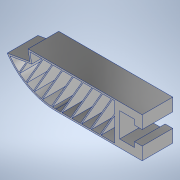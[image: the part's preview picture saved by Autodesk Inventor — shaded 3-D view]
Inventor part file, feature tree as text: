
AUTODESK INVENTOR PART (.ipt)
format: ipt  version: 2022 (Build 260153000, 153)  size: 298,496 bytes
history: native  units: mm
features: extrude x5, sketch x3, fillet x1, shell x1, projected_geometry x1
ambient origin geometry x8: Origin, YZ Plane, XZ Plane, XY Plane, X Axis, Y Axis, Z Axis, Center Point
bodies: Body1 (feature_tree)
feature tree (11):
  extrude  "Extrusion2"  Depth=5.8mm
  extrude  "Extrusion5"  Depth=12.0mm TaperAngle=0.0deg
  fillet  "Fillet2"  Radius=45.0mm
  shell  "Shell1"  Thickness=15.6mm
  extrude  "Extrusion7"  TaperAngle=0.0deg  [1 undecoded]
  extrude  "Extrusion8"  Depth=5.6mm
  extrude  "Extrusion9"  Depth=9.6mm
  sketch  "Sketch8"  dims[d41=5.8mm d48=44.0mm]
  sketch  "Sketch13"  dims[d50=3.0mm d56=12.0mm d57=0.0mm d63=45.0mm d67=15.6mm d71=0.0mm]
  sketch  "Sketch14"  dims[d80=17.453293mm d82=0.0mm d83=0.0mm d87=5.6mm d88=9.6mm d95=4.0mm d96=9.0mm d97=15.6mm d98=23.0mm d99=0.62mm d100=12.0mm d101=0.0mm d102=10.747401mm d103=12.0mm d104=0.0mm d105=0.38mm d1=0.38mm d127=12.0mm d128=0.0mm d130=120.0deg d132=120.0deg d133=0.38mm d135=0.38mm d136=0.38mm d137=0.38mm d138=0.38mm d139=0.38mm d140=0.38mm d141=0.38mm d142=3.81mm d143=0.38mm d144=3.81mm d145=3.81mm d146=3.81mm d147=3.81mm d148=3.81mm d152=120.0deg d153=3.81mm d154=3.81mm d155=3.81mm]
  projected_geometry  "Projected Loop1"
note: 1 required parameter value undecoded (feature->parameter linkage not recoverable at this tier; creation-order binding heuristic only, values carry confidence <= 0.55)
